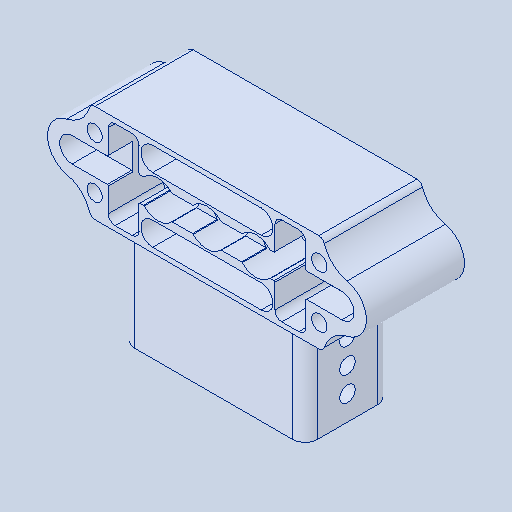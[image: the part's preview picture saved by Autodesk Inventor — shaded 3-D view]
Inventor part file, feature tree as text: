
AUTODESK INVENTOR PART (.ipt)
format: ipt  version: 2023.4 (Build 274418000, 418)  size: 476,160 bytes
history: native  units: in
note: dims shown in document units (in); Inventor stores cm internally (conversion verified against a paired STEP export)
features: fillet x1
ambient origin geometry x8: Origin, YZ Plane, XZ Plane, XY Plane, X Axis, Y Axis, Z Axis, Center Point
bodies: Solid1 (feature_tree)
feature tree (1):
  fillet  "Fillet6"  [1 undecoded]
note: 1 required parameter value undecoded (feature->parameter linkage not recoverable at this tier; creation-order binding heuristic only, values carry confidence <= 0.55)
